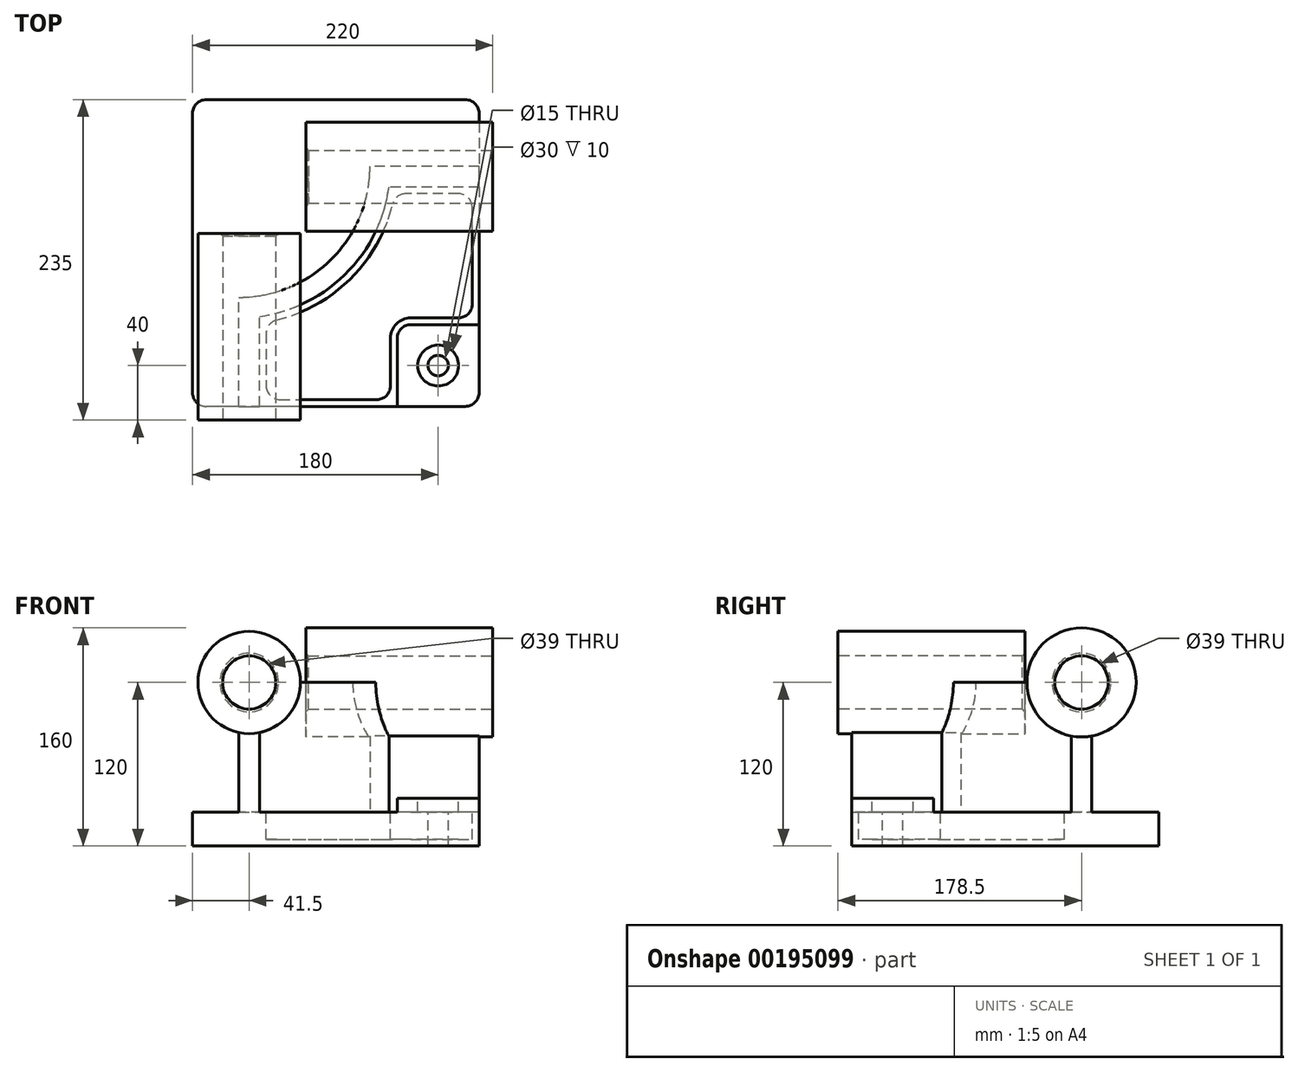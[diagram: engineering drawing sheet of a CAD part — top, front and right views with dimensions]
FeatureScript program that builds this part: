
annotation { "Feature Type Name" : "Feature", "Feature Type Description" : "" }
export const myFeature = defineFeature(function(context is Context, id is Id, definition is map)
    precondition{}
    {
        {
            var Q0;
            Q0=qCreatedBy(makeId("Top.planeOp"),FACE);
            var sketch = newSketch(context, id + "F0", { "sketchPlane" : qUnion([Q0])});
            skLineSegment(sketch, "E0.bottom", {"start": v(105, 112.5) * mm, "end": v(-105, 112.5) * mm});
            skLineSegment(sketch, "E0.top", {"start": v(105, -112.5) * mm, "end": v(-105, -112.5) * mm});
            skLineSegment(sketch, "E0.left", {"start": v(105, 112.5) * mm, "end": v(105, -112.5) * mm});
            skLineSegment(sketch, "E0.right", {"start": v(-105, 112.5) * mm, "end": v(-105, -112.5) * mm});
            skPoint(sketch, "E0.middle", {"position": v(0, 0) * mm});
            skSolve(sketch);
        }
        {
            var Q0;
            Q0 = qSketchRegion(id + "F0", true);
            extrude(context, id + "F1", {"entities" : qUnion([Q0]), "depth" : 25 * mm});
        }
        {
            var Q0;
            Q0=makeQuery(id+"F1.opExtrude","CAP_FACE",FACE,{"disambiguationData":[OSD([sQuery(id+"F0.wireOp",EDGE,"E0.bottom"),sQuery(id+"F0.wireOp",EDGE,"E0.top"),sQuery(id+"F0.wireOp",EDGE,"E0.left"),sQuery(id+"F0.wireOp",EDGE,"E0.right")])],"isStart":false});
            var sketch = newSketch(context, id + "F2", { "sketchPlane" : qUnion([Q0])});
            skLineSegment(sketch, "E1", {"start": v(-71, -112.5) * mm, "end": v(-71, -32.5) * mm});
            skLineSegment(sketch, "E2", {"start": v(105, 63.5) * mm, "end": v(25, 63.5) * mm});
            skArc(sketch, "E3", {"start": v(-71, -32.5) * mm, "mid": v(-3.12, -4.38) * mm, "end": v(25, 63.5) * mm});
            skLineSegment(sketch, "E4", {"start": v(-71, 63.5) * mm, "end": v(25, 63.5) * mm, "construction": true});
            skLineSegment(sketch, "E5", {"start": v(-71, 63.5) * mm, "end": v(-71, -32.5) * mm, "construction": true});
            skLineSegment(sketch, "E6.0", {"start": v(-56, -112.5) * mm, "end": v(-56, -46.48) * mm});
            skArc(sketch, "E6.1", {"start": v(-56, -46.48) * mm, "mid": v(7.49, -14.99) * mm, "end": v(38.98, 48.5) * mm});
            skLineSegment(sketch, "E6.2", {"start": v(105, 48.5) * mm, "end": v(38.98, 48.5) * mm});
            skSolve(sketch);
        }
        {
            var Q0;
            Q0 = qSketchRegion(id + "F2", true);
            var Q1;
            {var subQ2=sQuery(id+"F2.wireOp",EDGE,"E1");Q1=makeQuery(id+"F2.imprint","IMPRINT",FACE,{"disambiguationData":[TD([[makeQuery(id+"F2.imprint","IMPRINT",EDGE,{"derivedFrom":subQ2}),-1.0]])]});}
            extrude(context, id + "F3", {"entities" : qUnion([Q0, Q1]), "operationType" : NewBodyOperationType.ADD, "depth" : 95 * mm});
        }
        {
            var Q0;
            {var subQ0=sQuery(id+"F0.wireOp",EDGE,"E0.top");Q0=makeQuery(id+"F3.boolean.opBoolean","MERGE",FACE,{"derivedFrom":[makeQuery(id+"F1.opExtrude","SWEPT_FACE",FACE,{"disambiguationData":[OSD([subQ0])]}),makeQuery(id+"F3.opExtrude","SWEPT_FACE",FACE,{"disambiguationData":[OSD([subQ0])]})]});}
            var sketch = newSketch(context, id + "F4", { "sketchPlane" : qUnion([Q0])});
            skCircle(sketch, "E7", {"center": v(-63.5, 120) * mm, "radius": 37.5 * mm});
            skSolve(sketch);
        }
        {
            var Q0;
            Q0 = qSketchRegion(id + "F4", true);
            extrude(context, id + "F5", {"entities" : qUnion([Q0]), "operationType" : NewBodyOperationType.ADD, "depth" : 10 * mm, "hasSecondDirection" : true, "secondDirectionOppositeDirection" : true, "secondDirectionDepth" : (137 - 10) * mm});
        }
        {
            var Q0;
            {var subQ0=sQuery(id+"F0.wireOp",EDGE,"E0.left");Q0=makeQuery(id+"F3.boolean.opBoolean","MERGE",FACE,{"derivedFrom":[makeQuery(id+"F1.opExtrude","SWEPT_FACE",FACE,{"disambiguationData":[OSD([subQ0])]}),makeQuery(id+"F3.opExtrude","SWEPT_FACE",FACE,{"disambiguationData":[OSD([subQ0])]})]});}
            var sketch = newSketch(context, id + "F6", { "sketchPlane" : qUnion([Q0])});
            skCircle(sketch, "E8", {"center": v(56, 120) * mm, "radius": 40 * mm});
            skSolve(sketch);
        }
        {
            var Q0;
            Q0 = qSketchRegion(id + "F6", true);
            extrude(context, id + "F7", {"entities" : qUnion([Q0]), "operationType" : NewBodyOperationType.ADD, "depth" : 10 * mm, "hasSecondDirection" : true, "secondDirectionOppositeDirection" : true, "secondDirectionDepth" : (137 - 10) * mm});
        }
        {
            var Q0;
            {var subQ0=sQuery(id+"F0.wireOp",EDGE,"E0.left");var subQ1=sQuery(id+"F0.wireOp",EDGE,"E0.top");Q0=makeQuery(id+"F3.boolean.opBoolean","SPLIT",FACE,{"disambiguationData":[TD([makeQuery(id+"F3.opExtrude","SWEPT_FACE",FACE,{"disambiguationData":[OSD([sQuery(id+"F2.wireOp",EDGE,"E6.0")])]})])],"derivedFrom":makeQuery(id+"F1.opExtrude","CAP_FACE",FACE,{"disambiguationData":[OSD([sQuery(id+"F0.wireOp",EDGE,"E0.bottom"),subQ1,subQ0,sQuery(id+"F0.wireOp",EDGE,"E0.right")])],"isStart":false})});}
            var sketch = newSketch(context, id + "F8", { "sketchPlane" : qUnion([Q0])});
            skLineSegment(sketch, "E9.bottom", {"start": v(105, -112.5) * mm, "end": v(45, -112.5) * mm});
            skLineSegment(sketch, "E9.top", {"start": v(105, -52.5) * mm, "end": v(45, -52.5) * mm});
            skLineSegment(sketch, "E9.left", {"start": v(105, -112.5) * mm, "end": v(105, -52.5) * mm});
            skLineSegment(sketch, "E9.right", {"start": v(45, -112.5) * mm, "end": v(45, -52.5) * mm});
            skSolve(sketch);
        }
        {
            var Q0;
            Q0 = qSketchRegion(id + "F8", true);
            extrude(context, id + "F9", {"entities" : qUnion([Q0]), "operationType" : NewBodyOperationType.ADD, "depth" : 10 * mm});
        }
        {
            var Q0;
            Q0=makeQuery(id+"F9.opExtrude","SWEPT_EDGE",EDGE,{"disambiguationData":[OSD([sQuery(id+"F8.wireOp",EDGE,"E9.top"),sQuery(id+"F8.wireOp",EDGE,"E9.right")])]});
            fillet(context, id + "F10", {"entities" : qUnion([Q0]), "radius" : 10 * mm, "tangentPropagation" : true, "allowEdgeOverflow" : false});
        }
        {
            var Q0;
            {var subQ0=sQuery(id+"F0.wireOp",EDGE,"E0.left");var subQ1=sQuery(id+"F0.wireOp",EDGE,"E0.top");Q0=makeQuery(id+"F3.boolean.opBoolean","SPLIT",FACE,{"disambiguationData":[TD([makeQuery(id+"F3.opExtrude","SWEPT_FACE",FACE,{"disambiguationData":[OSD([sQuery(id+"F2.wireOp",EDGE,"E6.0")])]})])],"derivedFrom":makeQuery(id+"F1.opExtrude","CAP_FACE",FACE,{"disambiguationData":[OSD([sQuery(id+"F0.wireOp",EDGE,"E0.bottom"),subQ1,subQ0,sQuery(id+"F0.wireOp",EDGE,"E0.right")])],"isStart":false})});}
            var sketch = newSketch(context, id + "F11", { "sketchPlane" : qUnion([Q0])});
            skLineSegment(sketch, "E10.0", {"start": v(-51, -50.76) * mm, "end": v(-51, -107.5) * mm});
            skArc(sketch, "E10.1", {"start": v(43.26, 43.5) * mm, "mid": v(11.02, -18.52) * mm, "end": v(-51, -50.76) * mm});
            skLineSegment(sketch, "E10.2", {"start": v(-51, -107.5) * mm, "end": v(40, -107.5) * mm});
            skLineSegment(sketch, "E10.3", {"start": v(100, 43.5) * mm, "end": v(43.26, 43.5) * mm});
            skLineSegment(sketch, "E10.4", {"start": v(40, -107.5) * mm, "end": v(40, -62.5) * mm});
            skArc(sketch, "E10.5", {"start": v(40, -62.5) * mm, "mid": v(44.4, -51.9) * mm, "end": v(55, -47.5) * mm});
            skLineSegment(sketch, "E10.6", {"start": v(55, -47.5) * mm, "end": v(100, -47.5) * mm});
            skLineSegment(sketch, "E10.7", {"start": v(100, -47.5) * mm, "end": v(100, 43.5) * mm});
            skSolve(sketch);
        }
        {
            var Q0;
            Q0 = qSketchRegion(id + "F11", true);
            extrude(context, id + "F12", {"entities" : qUnion([Q0]), "operationType" : NewBodyOperationType.REMOVE, "oppositeDirection" : true, "depth" : 20 * mm});
        }
        {
            var Q0;
            Q0=makeQuery(id+"F9.opExtrude","CAP_FACE",FACE,{"disambiguationData":[OSD([sQuery(id+"F8.wireOp",EDGE,"E9.bottom"),sQuery(id+"F8.wireOp",EDGE,"E9.top"),sQuery(id+"F8.wireOp",EDGE,"E9.left"),sQuery(id+"F8.wireOp",EDGE,"E9.right")])],"isStart":false});
            var sketch = newSketch(context, id + "F13", { "sketchPlane" : qUnion([Q0])});
            skCircle(sketch, "E11", {"center": v(75, -82.5) * mm, "radius": 15 * mm});
            skSolve(sketch);
        }
        {
            var Q0;
            Q0=sQuery(id+"F13.wireOp",VERTEX,"E11.center");
            var Q1;
            Q1=makeQuery(id+"F1.opExtrude","SWEPT_BODY",BODY,{"disambiguationData":[OSD([sQuery(id+"F0.wireOp",EDGE,"E0.bottom"),sQuery(id+"F0.wireOp",EDGE,"E0.top"),sQuery(id+"F0.wireOp",EDGE,"E0.left"),sQuery(id+"F0.wireOp",EDGE,"E0.right")])]});
            hole(context, id + "F14", {"style" : HoleStyle.C_BORE, "endStyle" : HoleEndStyle.THROUGH, "holeDiameter" : 15 * mm, "cBoreDiameter" : 30 * mm, "cBoreDepth" : 10 * mm, "locations" : qUnion([Q0]), "scope" : qUnion([Q1]), "isTappedThrough" : true});
        }
        {
            var Q0;
            Q0=makeQuery(id+"F12.boolean.opBoolean","COPY",EDGE,{"derivedFrom":makeQuery(id+"F12.opExtrude","SWEPT_EDGE",EDGE,{"disambiguationData":[OSD([sQuery(id+"F11.wireOp",EDGE,"E10.0"),sQuery(id+"F11.wireOp",EDGE,"E10.1")])]})});
            var Q1;
            Q1=makeQuery(id+"F12.boolean.opBoolean","COPY",EDGE,{"derivedFrom":makeQuery(id+"F12.opExtrude","SWEPT_EDGE",EDGE,{"disambiguationData":[OSD([sQuery(id+"F11.wireOp",EDGE,"E10.1"),sQuery(id+"F11.wireOp",EDGE,"E10.3")])]})});
            var Q2;
            Q2=makeQuery(id+"F12.boolean.opBoolean","COPY",EDGE,{"derivedFrom":makeQuery(id+"F12.opExtrude","SWEPT_EDGE",EDGE,{"disambiguationData":[OSD([sQuery(id+"F11.wireOp",EDGE,"E10.3"),sQuery(id+"F11.wireOp",EDGE,"E10.7")])]})});
            var Q3;
            Q3=makeQuery(id+"F12.boolean.opBoolean","COPY",EDGE,{"derivedFrom":makeQuery(id+"F12.opExtrude","SWEPT_EDGE",EDGE,{"disambiguationData":[OSD([sQuery(id+"F11.wireOp",EDGE,"E10.2"),sQuery(id+"F11.wireOp",EDGE,"E10.4")])]})});
            var Q4;
            Q4=makeQuery(id+"F12.boolean.opBoolean","COPY",EDGE,{"derivedFrom":makeQuery(id+"F12.opExtrude","SWEPT_EDGE",EDGE,{"disambiguationData":[OSD([sQuery(id+"F11.wireOp",EDGE,"E10.6"),sQuery(id+"F11.wireOp",EDGE,"E10.7")])]})});
            var Q5;
            Q5=makeQuery(id+"F12.boolean.opBoolean","COPY",EDGE,{"derivedFrom":makeQuery(id+"F12.opExtrude","SWEPT_EDGE",EDGE,{"disambiguationData":[OSD([sQuery(id+"F11.wireOp",EDGE,"E10.0"),sQuery(id+"F11.wireOp",EDGE,"E10.2")])]})});
            fillet(context, id + "F15", {"entities" : qUnion([Q0, Q1, Q2, Q3, Q4, Q5]), "radius" : 10 * mm, "tangentPropagation" : true, "allowEdgeOverflow" : false});
        }
        {
            var Q0;
            Q0=makeQuery(id+"F5.opExtrude","CAP_FACE",FACE,{"disambiguationData":[OSD([sQuery(id+"F4.wireOp",EDGE,"E7")])],"isStart":false});
            var sketch = newSketch(context, id + "F16", { "sketchPlane" : qUnion([Q0])});
            skCircle(sketch, "E12", {"center": v(-63.5, 120) * mm, "radius": 19.5 * mm});
            skSolve(sketch);
        }
        {
            var Q0;
            Q0 = qSketchRegion(id + "F16", true);
            extrude(context, id + "F17", {"entities" : qUnion([Q0]), "operationType" : NewBodyOperationType.REMOVE, "endBound" : BoundingType.THROUGH_ALL, "oppositeDirection" : true, "depth" : 25 * mm});
        }
        {
            var Q0;
            Q0=makeQuery(id+"F7.opExtrude","CAP_FACE",FACE,{"disambiguationData":[OSD([sQuery(id+"F6.wireOp",EDGE,"E8")])],"isStart":false});
            var sketch = newSketch(context, id + "F18", { "sketchPlane" : qUnion([Q0])});
            skCircle(sketch, "E13", {"center": v(56, 120) * mm, "radius": 19.5 * mm});
            skSolve(sketch);
        }
        {
            var Q0;
            Q0 = qSketchRegion(id + "F18", true);
            extrude(context, id + "F19", {"entities" : qUnion([Q0]), "operationType" : NewBodyOperationType.REMOVE, "endBound" : BoundingType.THROUGH_ALL, "oppositeDirection" : true, "depth" : 25 * mm});
        }
        {
            var Q0;
            Q0=makeQuery(id+"F17.boolean.opBoolean","COPY",EDGE,{"derivedFrom":makeQuery(id+"F17.opExtrude","CAP_EDGE",EDGE,{"disambiguationData":[OSD([sQuery(id+"F16.wireOp",EDGE,"E12")])],"isStart":true})});
            var Q1;
            Q1=makeQuery(id+"F19.boolean.opBoolean","COPY",EDGE,{"derivedFrom":makeQuery(id+"F19.opExtrude","CAP_EDGE",EDGE,{"disambiguationData":[OSD([sQuery(id+"F18.wireOp",EDGE,"E13")])],"isStart":true})});
            var Q2;
            Q2=makeQuery(id+"F19.boolean.opBoolean","INTERSECT",EDGE,{"derivedFrom":[makeQuery(id+"F7.opExtrude","CAP_FACE",FACE,{"disambiguationData":[OSD([sQuery(id+"F6.wireOp",EDGE,"E8")])],"isStart":true}),makeQuery(id+"F19.opExtrude","SWEPT_FACE",FACE,{"disambiguationData":[OSD([sQuery(id+"F18.wireOp",EDGE,"E13")])]})]});
            var Q3;
            Q3=makeQuery(id+"F17.boolean.opBoolean","INTERSECT",EDGE,{"derivedFrom":[makeQuery(id+"F5.opExtrude","CAP_FACE",FACE,{"disambiguationData":[OSD([sQuery(id+"F4.wireOp",EDGE,"E7")])],"isStart":true}),makeQuery(id+"F17.opExtrude","SWEPT_FACE",FACE,{"disambiguationData":[OSD([sQuery(id+"F16.wireOp",EDGE,"E12")])]})]});
            chamfer(context, id + "F20", {"entities" : qUnion([Q0, Q1, Q2, Q3]), "width" : 2 * mm, "tangentPropagation" : true});
        }
        {
            var Q0;
            Q0=makeQuery(id+"F1.opExtrude","SWEPT_EDGE",EDGE,{"disambiguationData":[OSD([sQuery(id+"F0.wireOp",EDGE,"E0.bottom"),sQuery(id+"F0.wireOp",EDGE,"E0.right")])]});
            var Q1;
            Q1=makeQuery(id+"F1.opExtrude","SWEPT_EDGE",EDGE,{"disambiguationData":[OSD([sQuery(id+"F0.wireOp",EDGE,"E0.top"),sQuery(id+"F0.wireOp",EDGE,"E0.right")])]});
            var Q2;
            Q2=makeQuery(id+"F1.opExtrude","SWEPT_EDGE",EDGE,{"disambiguationData":[OSD([sQuery(id+"F0.wireOp",EDGE,"E0.bottom"),sQuery(id+"F0.wireOp",EDGE,"E0.left")])]});
            var Q3;
            Q3=makeQuery(id+"F9.boolean.opBoolean","MERGE",EDGE,{"derivedFrom":[makeQuery(id+"F1.opExtrude","SWEPT_EDGE",EDGE,{"disambiguationData":[OSD([sQuery(id+"F0.wireOp",EDGE,"E0.top"),sQuery(id+"F0.wireOp",EDGE,"E0.left")])]}),makeQuery(id+"F9.opExtrude","SWEPT_EDGE",EDGE,{"disambiguationData":[OSD([sQuery(id+"F8.wireOp",EDGE,"E9.bottom"),sQuery(id+"F8.wireOp",EDGE,"E9.left")])]})]});
            fillet(context, id + "F21", {"entities" : qUnion([Q0, Q1, Q2, Q3]), "radius" : 10 * mm, "tangentPropagation" : true, "allowEdgeOverflow" : false});
        }
    });
